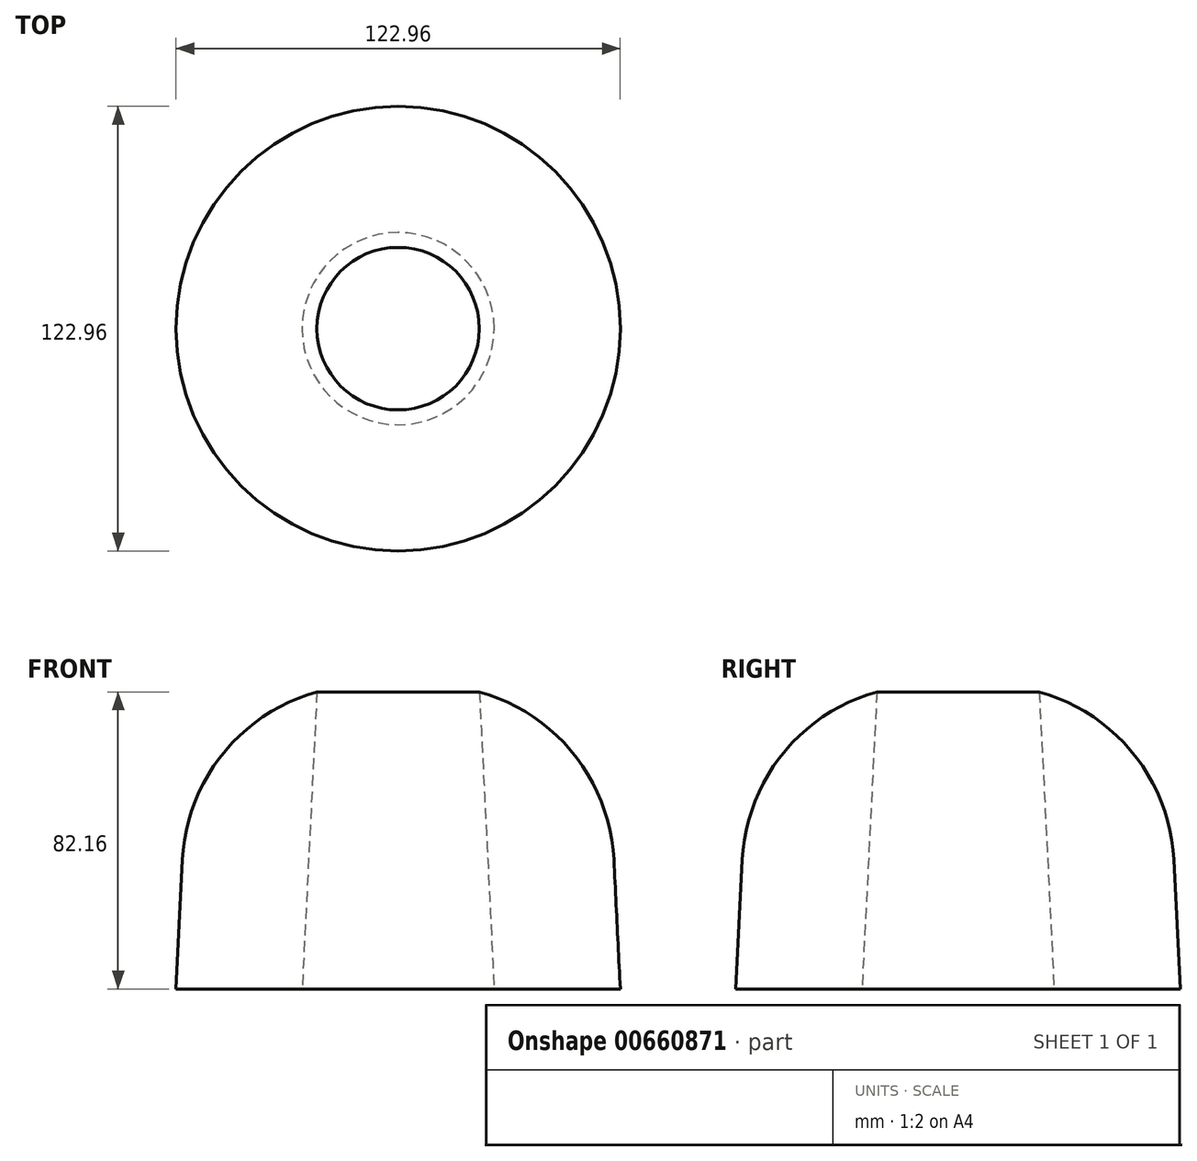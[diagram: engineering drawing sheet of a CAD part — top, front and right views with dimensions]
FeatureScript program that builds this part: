
annotation { "Feature Type Name" : "Feature", "Feature Type Description" : "" }
export const myFeature = defineFeature(function(context is Context, id is Id, definition is map)
    precondition{}
    {
        {
            var Q0;
            Q0=qCreatedBy(makeId("Front.planeOp"),FACE);
            var sketch = newSketch(context, id + "F0", { "sketchPlane" : qUnion([Q0])});
            skLineSegment(sketch, "E0", {"start": v(0, 84.96) * mm, "end": v(0, -59.4) * mm, "construction": true});
            skLineSegment(sketch, "E1", {"start": v(-57.39, 36.93) * mm, "end": v(-22.48, 36.93) * mm});
            skLineSegment(sketch, "E2", {"start": v(-22.48, 36.93) * mm, "end": v(-26.57, -45.23) * mm});
            skLineSegment(sketch, "E3", {"start": v(-26.57, -45.23) * mm, "end": v(-61.48, -45.23) * mm});
            skLineSegment(sketch, "E4", {"start": v(-61.48, -45.23) * mm, "end": v(-57.39, 36.93) * mm});
            skSolve(sketch);
        }
        {
            var Q0;
            Q0 = qSketchRegion(id + "F0", true);
            var Q1;
            Q1=makeQuery(id+"F0.imprint","IMPRINT",FACE,{"disambiguationData":[TD([[makeQuery(id+"F0.imprint","IMPRINT",EDGE,{"derivedFrom":sQuery(id+"F0.wireOp",EDGE,"E1")}),-1.0]])]});
            var Q2;
            Q2=sQuery(id+"F0.wireOp",EDGE,"E0");
            revolve(context, id + "F1", {"entities" : qUnion([Q0, Q1]), "axis" : qUnion([Q2]), "revolveType" : RevolveType.FULL});
        }
        {
            var Q0;
            Q0=makeQuery(id+"F1.opRevolve","SWEPT_EDGE",EDGE,{"disambiguationData":[OSD([sQuery(id+"F0.wireOp",EDGE,"E1"),sQuery(id+"F0.wireOp",EDGE,"E4")])]});
            fillet(context, id + "F2", {"entities" : qUnion([Q0]), "radius" : 50.8 * mm, "tangentPropagation" : true, "allowEdgeOverflow" : false});
        }
    });
